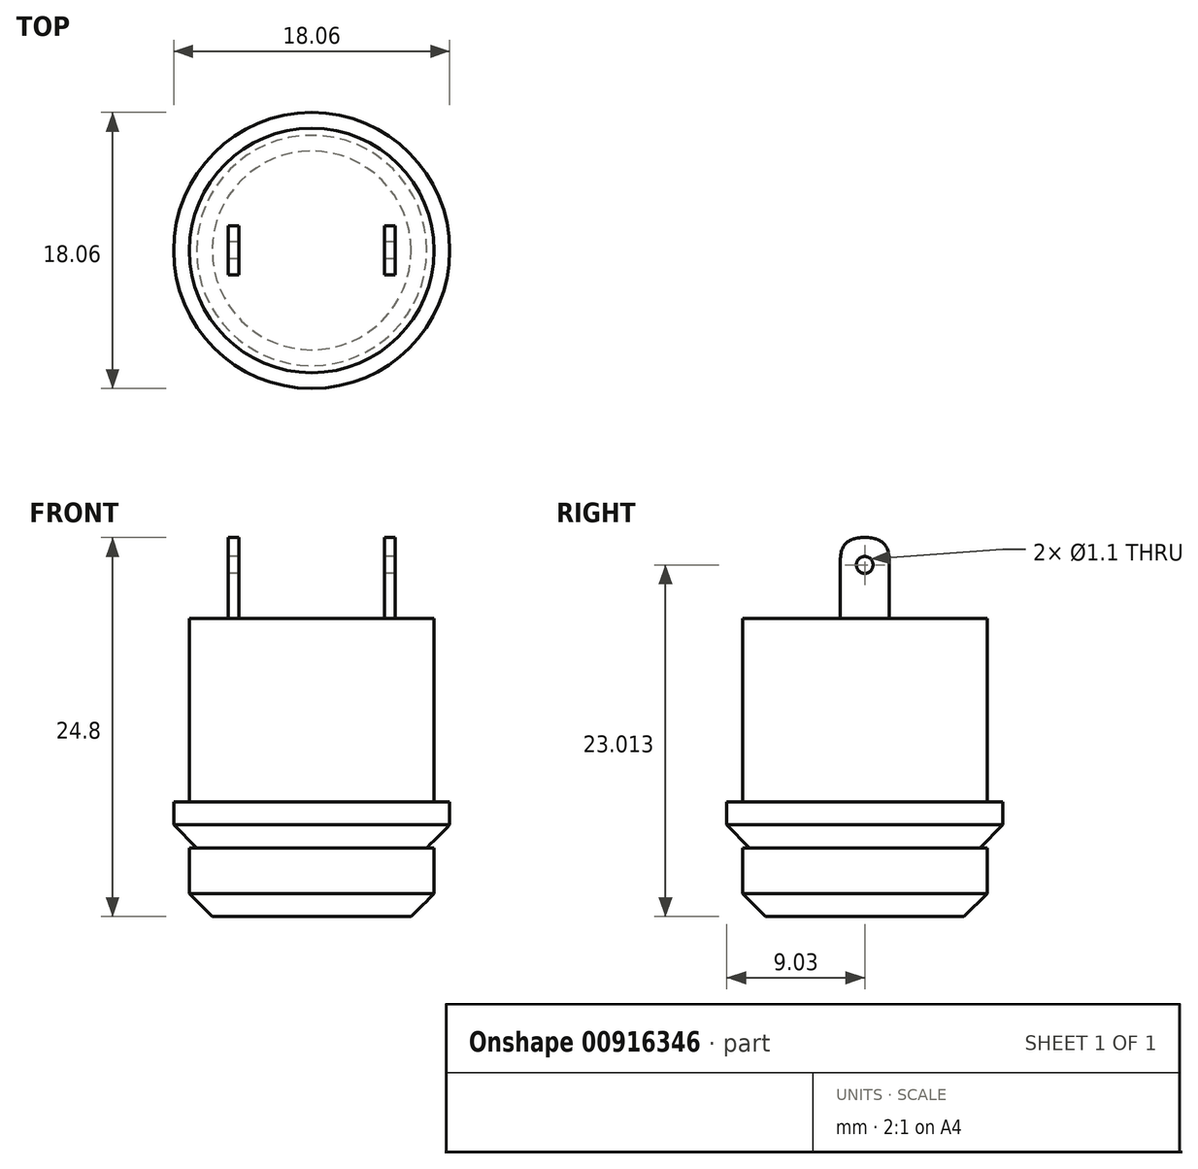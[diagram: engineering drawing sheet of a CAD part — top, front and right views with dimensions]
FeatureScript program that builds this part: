
annotation { "Feature Type Name" : "Feature", "Feature Type Description" : "" }
export const myFeature = defineFeature(function(context is Context, id is Id, definition is map)
    precondition{}
    {
        {
            var Q0;
            Q0=qCreatedBy(makeId("Top.planeOp"),FACE);
            var sketch = newSketch(context, id + "F0", { "sketchPlane" : qUnion([Q0])});
            skCircle(sketch, "E0", {"center": v(0, 0) * mm, "radius": 8 * mm});
            skCircle(sketch, "E1", {"center": v(0, 0) * mm, "radius": 9.03 * mm});
            skSolve(sketch);
        }
        {
            var Q0;
            Q0=makeQuery(id+"F0.imprint","IMPRINT",FACE,{"disambiguationData":[TD([[makeQuery(id+"F0.imprint","IMPRINT",EDGE,{"derivedFrom":sQuery(id+"F0.wireOp",EDGE,"E0")}),1.0]])]});
            extrude(context, id + "F1", {"entities" : qUnion([Q0]), "depth" : 15 * mm, "offsetDistance" : 25 * mm});
        }
        {
            var Q0;
            Q0=makeQuery(id+"F0.imprint","IMPRINT",FACE,{"disambiguationData":[TD([[makeQuery(id+"F0.imprint","IMPRINT",EDGE,{"derivedFrom":sQuery(id+"F0.wireOp",EDGE,"E0")}),-1.0]])]});
            var Q1;
            Q1=makeQuery(id+"F0.imprint","IMPRINT",FACE,{"disambiguationData":[TD([[makeQuery(id+"F0.imprint","IMPRINT",EDGE,{"derivedFrom":sQuery(id+"F0.wireOp",EDGE,"E0")}),1.0]])]});
            extrude(context, id + "F2", {"entities" : qUnion([Q0, Q1]), "operationType" : NewBodyOperationType.ADD, "depth" : 3 * mm, "offsetDistance" : 25 * mm});
        }
        {
            var Q0;
            Q0=makeQuery(id+"F0.imprint","IMPRINT",FACE,{"disambiguationData":[TD([[makeQuery(id+"F0.imprint","IMPRINT",EDGE,{"derivedFrom":sQuery(id+"F0.wireOp",EDGE,"E0")}),1.0]])]});
            extrude(context, id + "F3", {"entities" : qUnion([Q0]), "oppositeDirection" : true, "depth" : 4.5 * mm, "offsetDistance" : 25 * mm});
        }
        {
            var Q0;
            Q0=makeQuery(id+"F3.opExtrude","CAP_EDGE",EDGE,{"disambiguationData":[OSD([sQuery(id+"F0.wireOp",EDGE,"E0")])],"isStart":false});
            var Q1;
            Q1=makeQuery(id+"F2.opExtrude","CAP_EDGE",EDGE,{"disambiguationData":[OSD([sQuery(id+"F0.wireOp",EDGE,"E1")])],"isStart":true});
            chamfer(context, id + "F4", {"entities" : qUnion([Q0, Q1]), "width" : 1.5 * mm, "tangentPropagation" : true});
        }
        {
            var Q0;
            Q0=makeQuery(id+"F1.opExtrude","CAP_FACE",FACE,{"disambiguationData":[OSD([sQuery(id+"F0.wireOp",EDGE,"E0")])],"isStart":false});
            var sketch = newSketch(context, id + "F5", { "sketchPlane" : qUnion([Q0])});
            skLineSegment(sketch, "E2", {"start": v(0, 8) * mm, "end": v(0, -8) * mm, "construction": true});
            skLineSegment(sketch, "E3.bottom", {"start": v(-5.45, 1.6) * mm, "end": v(-4.75, 1.6) * mm});
            skLineSegment(sketch, "E3.top", {"start": v(-5.45, -1.6) * mm, "end": v(-4.75, -1.6) * mm});
            skLineSegment(sketch, "E3.left", {"start": v(-5.45, 1.6) * mm, "end": v(-5.45, -1.6) * mm});
            skLineSegment(sketch, "E3.right", {"start": v(-4.75, 1.6) * mm, "end": v(-4.75, -1.6) * mm});
            skLineSegment(sketch, "E4.MirrorCS", {"start": v(5.45, -1.6) * mm, "end": v(4.75, -1.6) * mm});
            skLineSegment(sketch, "E5.MirrorCS", {"start": v(5.45, 1.6) * mm, "end": v(5.45, -1.6) * mm});
            skLineSegment(sketch, "E6.MirrorCS", {"start": v(5.45, 1.6) * mm, "end": v(4.75, 1.6) * mm});
            skLineSegment(sketch, "E7.MirrorCS", {"start": v(4.75, 1.6) * mm, "end": v(4.75, -1.6) * mm});
            skLineSegment(sketch, "E8", {"start": v(-8, 0) * mm, "end": v(8, 0) * mm, "construction": true});
            skPoint(sketch, "E8.startSnap0", {"position": v(-5.45, 0) * mm});
            skSolve(sketch);
        }
        {
            var Q0;
            Q0=makeQuery(id+"F5.imprint","IMPRINT",FACE,{"disambiguationData":[TD([[makeQuery(id+"F5.imprint","IMPRINT",EDGE,{"derivedFrom":sQuery(id+"F5.wireOp",EDGE,"E3.bottom")}),-1.0]])]});
            var Q1;
            Q1=makeQuery(id+"F5.imprint","IMPRINT",FACE,{"disambiguationData":[TD([[makeQuery(id+"F5.imprint","IMPRINT",EDGE,{"derivedFrom":sQuery(id+"F5.wireOp",EDGE,"E4.MirrorCS")}),-1.0]])]});
            extrude(context, id + "F6", {"entities" : qUnion([Q0, Q1]), "operationType" : NewBodyOperationType.ADD, "depth" : 5.3 * mm, "offsetDistance" : 25 * mm});
        }
        {
            var Q0;
            Q0=makeQuery(id+"F6.opExtrude","SWEPT_FACE",FACE,{"disambiguationData":[OSD([sQuery(id+"F5.wireOp",EDGE,"E3.left")])]});
            var sketch = newSketch(context, id + "F7", { "sketchPlane" : qUnion([Q0])});
            skCircle(sketch, "E9", {"center": v(0, 18.51) * mm, "radius": 0.55 * mm});
            skSolve(sketch);
        }
        {
            var Q0;
            Q0=makeQuery(id+"F7.imprint","IMPRINT",FACE,{"disambiguationData":[TD([[makeQuery(id+"F7.imprint","IMPRINT",EDGE,{"derivedFrom":sQuery(id+"F7.wireOp",EDGE,"E9")}),1.0]])]});
            extrude(context, id + "F8", {"entities" : qUnion([Q0]), "operationType" : NewBodyOperationType.REMOVE, "oppositeDirection" : true, "depth" : 25 * mm, "offsetDistance" : 25 * mm});
        }
        {
            var Q0;
            Q0=makeQuery(id+"F6.opExtrude","CAP_EDGE",EDGE,{"disambiguationData":[OSD([sQuery(id+"F5.wireOp",EDGE,"E3.top")])],"isStart":false});
            var Q1;
            Q1=makeQuery(id+"F6.opExtrude","CAP_EDGE",EDGE,{"disambiguationData":[OSD([sQuery(id+"F5.wireOp",EDGE,"E3.bottom")])],"isStart":false});
            var Q2;
            Q2=makeQuery(id+"F6.opExtrude","CAP_EDGE",EDGE,{"disambiguationData":[OSD([sQuery(id+"F5.wireOp",EDGE,"E4.MirrorCS")])],"isStart":false});
            var Q3;
            Q3=makeQuery(id+"F6.opExtrude","CAP_EDGE",EDGE,{"disambiguationData":[OSD([sQuery(id+"F5.wireOp",EDGE,"E6.MirrorCS")])],"isStart":false});
            fillet(context, id + "F9", {"entities" : qUnion([Q0, Q1, Q2, Q3]), "radius" : 1.5 * mm, "tangentPropagation" : true, "rho" : 0.5, "crossSection" : FilletCrossSection.CONIC, "allowEdgeOverflow" : false});
        }
    });
